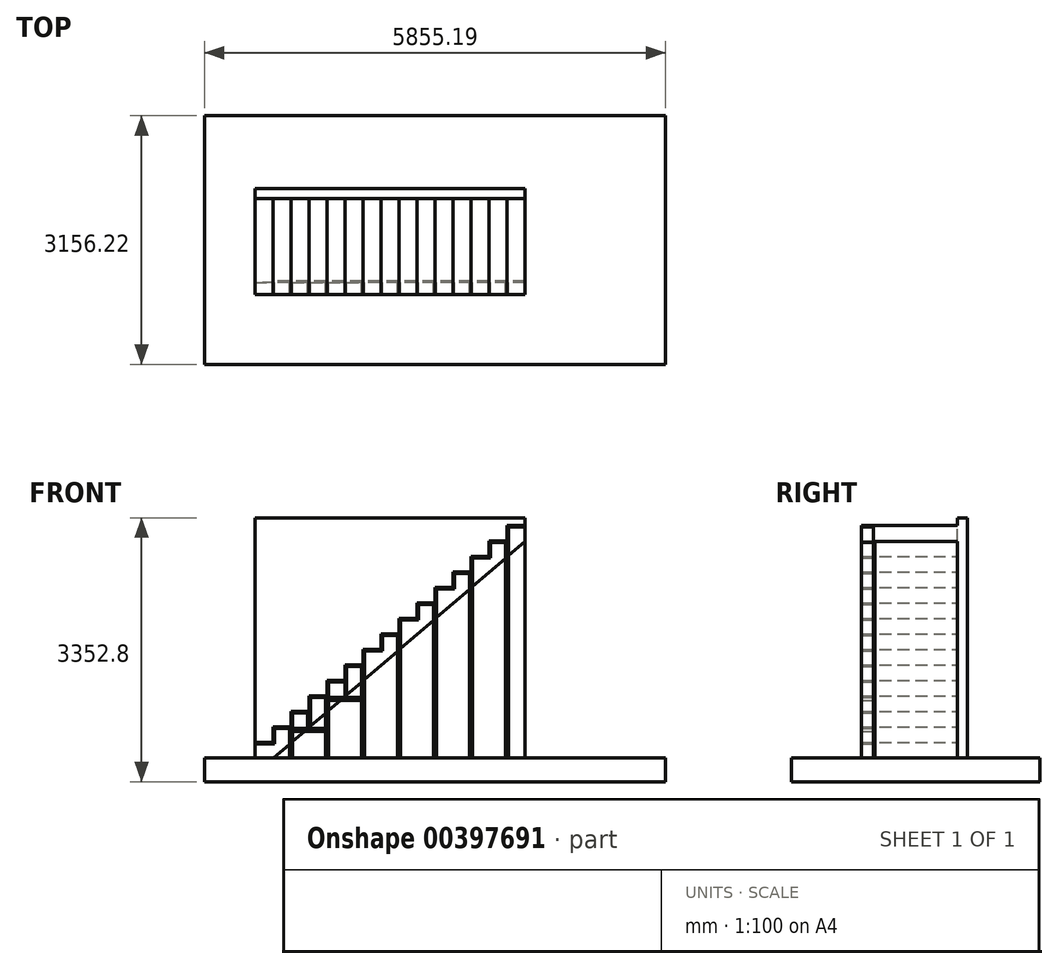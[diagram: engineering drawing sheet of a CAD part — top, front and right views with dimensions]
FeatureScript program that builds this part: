
annotation { "Feature Type Name" : "Feature", "Feature Type Description" : "" }
export const myFeature = defineFeature(function(context is Context, id is Id, definition is map)
    precondition{}
    {
        {
            var Q0;
            Q0=qCreatedBy(makeId("Front.planeOp"),FACE);
            var sketch = newSketch(context, id + "F0", { "sketchPlane" : qUnion([Q0])});
            skLineSegment(sketch, "E0", {"start": v(0, 0) * mm, "end": v(0, 196.85) * mm});
            skLineSegment(sketch, "E1", {"start": v(0, 196.85) * mm, "end": v(228.6, 196.85) * mm});
            skLineSegment(sketch, "E2", {"start": v(228.6, 196.85) * mm, "end": v(228.6, 393.7) * mm});
            skLineSegment(sketch, "E3", {"start": v(228.6, 393.7) * mm, "end": v(457.2, 393.7) * mm});
            skLineSegment(sketch, "E4", {"start": v(457.2, 393.7) * mm, "end": v(457.2, 590.55) * mm});
            skLineSegment(sketch, "E5", {"start": v(457.2, 590.55) * mm, "end": v(685.8, 590.55) * mm});
            skLineSegment(sketch, "E6", {"start": v(685.8, 590.55) * mm, "end": v(685.8, 787.4) * mm});
            skLineSegment(sketch, "E7", {"start": v(685.8, 787.4) * mm, "end": v(914.4, 787.4) * mm});
            skLineSegment(sketch, "E8", {"start": v(914.4, 787.4) * mm, "end": v(914.4, 984.25) * mm});
            skLineSegment(sketch, "E9", {"start": v(914.4, 984.25) * mm, "end": v(1143, 984.25) * mm});
            skLineSegment(sketch, "E10", {"start": v(1143, 984.25) * mm, "end": v(1143, 1181.1) * mm});
            skLineSegment(sketch, "E11", {"start": v(1143, 1181.1) * mm, "end": v(1371.6, 1181.1) * mm});
            skLineSegment(sketch, "E12", {"start": v(1371.6, 1181.1) * mm, "end": v(1371.6, 1377.95) * mm});
            skLineSegment(sketch, "E13", {"start": v(1371.6, 1377.95) * mm, "end": v(1600.2, 1377.95) * mm});
            skLineSegment(sketch, "E14", {"start": v(1600.2, 1377.95) * mm, "end": v(1600.2, 1574.8) * mm});
            skLineSegment(sketch, "E15", {"start": v(1600.2, 1574.8) * mm, "end": v(1828.8, 1574.8) * mm});
            skLineSegment(sketch, "E16", {"start": v(1828.8, 1574.8) * mm, "end": v(1828.8, 1771.65) * mm});
            skLineSegment(sketch, "E17", {"start": v(1828.8, 1771.65) * mm, "end": v(2057.4, 1771.65) * mm});
            skLineSegment(sketch, "E18", {"start": v(2057.4, 1771.65) * mm, "end": v(2057.4, 1968.5) * mm});
            skLineSegment(sketch, "E19", {"start": v(2057.4, 1968.5) * mm, "end": v(2286, 1968.5) * mm});
            skLineSegment(sketch, "E20", {"start": v(2286, 1968.5) * mm, "end": v(2286, 2165.35) * mm});
            skLineSegment(sketch, "E21", {"start": v(2286, 2165.35) * mm, "end": v(2514.6, 2165.35) * mm});
            skLineSegment(sketch, "E22", {"start": v(2514.6, 2165.35) * mm, "end": v(2514.6, 2362.2) * mm});
            skLineSegment(sketch, "E23", {"start": v(2514.6, 2362.2) * mm, "end": v(2743.2, 2362.2) * mm});
            skLineSegment(sketch, "E24", {"start": v(2743.2, 2362.2) * mm, "end": v(2743.2, 2559.05) * mm});
            skLineSegment(sketch, "E25", {"start": v(2743.2, 2559.05) * mm, "end": v(2971.8, 2559.05) * mm});
            skLineSegment(sketch, "E26", {"start": v(2971.8, 2559.05) * mm, "end": v(2971.8, 2755.9) * mm});
            skLineSegment(sketch, "E27", {"start": v(2971.8, 2755.9) * mm, "end": v(3200.4, 2755.9) * mm});
            skLineSegment(sketch, "E28", {"start": v(3200.4, 2755.9) * mm, "end": v(3200.4, 2952.75) * mm});
            skLineSegment(sketch, "E29", {"start": v(3200.4, 2952.75) * mm, "end": v(3429, 2952.75) * mm});
            skLineSegment(sketch, "E30", {"start": v(3429, 2952.75) * mm, "end": v(3429, 2747.37) * mm});
            skLineSegment(sketch, "E31", {"start": v(3200.4, 2952.75) * mm, "end": v(228.6, 393.7) * mm, "construction": true});
            skLineSegment(sketch, "E32", {"start": v(3429, 2747.37) * mm, "end": v(238.5, 0) * mm});
            skLineSegment(sketch, "E33", {"start": v(0, 0) * mm, "end": v(238.5, 0) * mm});
            skPoint(sketch, "E34.orphan", {"position": v(228.6, -8.53) * mm});
            skSolve(sketch);
        }
        {
            var Q0;
            Q0 = qSketchRegion(id + "F0", true);
            extrude(context, id + "F1", {"entities" : qUnion([Q0]), "depth" : 1066.8 * mm});
        }
        {
            var Q0;
            Q0=makeQuery(id+"F1.opExtrude","SWEPT_FACE",FACE,{"disambiguationData":[OSD([sQuery(id+"F0.wireOp",EDGE,"E33")])]});
            var sketch = newSketch(context, id + "F2", { "sketchPlane" : qUnion([Q0])});
            skLineSegment(sketch, "E35.bottom", {"start": v(0, 0) * mm, "end": v(3429, 0) * mm});
            skLineSegment(sketch, "E35.top", {"start": v(0, -127) * mm, "end": v(3429, -127) * mm});
            skLineSegment(sketch, "E35.left", {"start": v(0, 0) * mm, "end": v(0, -127) * mm});
            skLineSegment(sketch, "E35.right", {"start": v(3429, 0) * mm, "end": v(3429, -127) * mm});
            skSolve(sketch);
        }
        {
            var Q0;
            Q0=makeQuery(id+"F2.imprint","IMPRINT",FACE,{"disambiguationData":[TD([[makeQuery(id+"F2.imprint","IMPRINT",EDGE,{"derivedFrom":sQuery(id+"F2.wireOp",EDGE,"E35.top")}),1.0]])]});
            extrude(context, id + "F3", {"entities" : qUnion([Q0]), "operationType" : NewBodyOperationType.ADD, "oppositeDirection" : true, "depth" : 3048 * mm});
        }
        {
            var Q0;
            Q0=makeQuery(id+"F1.opExtrude","CAP_FACE",FACE,{"disambiguationData":[OSD([sQuery(id+"F0.wireOp",EDGE,"E0"),sQuery(id+"F0.wireOp",EDGE,"E1"),sQuery(id+"F0.wireOp",EDGE,"E2"),sQuery(id+"F0.wireOp",EDGE,"E3"),sQuery(id+"F0.wireOp",EDGE,"E4"),sQuery(id+"F0.wireOp",EDGE,"E5"),sQuery(id+"F0.wireOp",EDGE,"E6"),sQuery(id+"F0.wireOp",EDGE,"E7"),sQuery(id+"F0.wireOp",EDGE,"E8"),sQuery(id+"F0.wireOp",EDGE,"E9"),sQuery(id+"F0.wireOp",EDGE,"E10"),sQuery(id+"F0.wireOp",EDGE,"E11"),sQuery(id+"F0.wireOp",EDGE,"E12"),sQuery(id+"F0.wireOp",EDGE,"E13"),sQuery(id+"F0.wireOp",EDGE,"E14"),sQuery(id+"F0.wireOp",EDGE,"E15"),sQuery(id+"F0.wireOp",EDGE,"E16"),sQuery(id+"F0.wireOp",EDGE,"E17"),sQuery(id+"F0.wireOp",EDGE,"E18"),sQuery(id+"F0.wireOp",EDGE,"E19"),sQuery(id+"F0.wireOp",EDGE,"E20"),sQuery(id+"F0.wireOp",EDGE,"E21"),sQuery(id+"F0.wireOp",EDGE,"E22"),sQuery(id+"F0.wireOp",EDGE,"E23"),sQuery(id+"F0.wireOp",EDGE,"E24"),sQuery(id+"F0.wireOp",EDGE,"E25"),sQuery(id+"F0.wireOp",EDGE,"E26"),sQuery(id+"F0.wireOp",EDGE,"E27"),sQuery(id+"F0.wireOp",EDGE,"E28"),sQuery(id+"F0.wireOp",EDGE,"E29"),sQuery(id+"F0.wireOp",EDGE,"E30"),sQuery(id+"F0.wireOp",EDGE,"E32"),sQuery(id+"F0.wireOp",EDGE,"E33")])],"isStart":false});
            var sketch = newSketch(context, id + "F4", { "sketchPlane" : qUnion([Q0])});
            skLineSegment(sketch, "E36", {"start": v(238.5, 0) * mm, "end": v(3429, 2747.37) * mm});
            skLineSegment(sketch, "E37", {"start": v(3429, 2747.37) * mm, "end": v(3429, 0) * mm});
            skLineSegment(sketch, "E38", {"start": v(3429, 0) * mm, "end": v(238.5, 0) * mm});
            skSolve(sketch);
        }
        {
            var Q0;
            Q0=makeQuery(id+"F4.imprint","IMPRINT",FACE,{"disambiguationData":[TD([[makeQuery(id+"F4.imprint","IMPRINT",EDGE,{"derivedFrom":sQuery(id+"F4.wireOp",EDGE,"E36")}),1.0]])]});
            extrude(context, id + "F5", {"entities" : qUnion([Q0]), "oppositeDirection" : true, "depth" : 19.05 * mm});
        }
        {
            var Q0;
            Q0=makeQuery(id+"F1.opExtrude","CAP_FACE",FACE,{"disambiguationData":[OSD([sQuery(id+"F0.wireOp",EDGE,"E0"),sQuery(id+"F0.wireOp",EDGE,"E1"),sQuery(id+"F0.wireOp",EDGE,"E2"),sQuery(id+"F0.wireOp",EDGE,"E3"),sQuery(id+"F0.wireOp",EDGE,"E4"),sQuery(id+"F0.wireOp",EDGE,"E5"),sQuery(id+"F0.wireOp",EDGE,"E6"),sQuery(id+"F0.wireOp",EDGE,"E7"),sQuery(id+"F0.wireOp",EDGE,"E8"),sQuery(id+"F0.wireOp",EDGE,"E9"),sQuery(id+"F0.wireOp",EDGE,"E10"),sQuery(id+"F0.wireOp",EDGE,"E11"),sQuery(id+"F0.wireOp",EDGE,"E12"),sQuery(id+"F0.wireOp",EDGE,"E13"),sQuery(id+"F0.wireOp",EDGE,"E14"),sQuery(id+"F0.wireOp",EDGE,"E15"),sQuery(id+"F0.wireOp",EDGE,"E16"),sQuery(id+"F0.wireOp",EDGE,"E17"),sQuery(id+"F0.wireOp",EDGE,"E18"),sQuery(id+"F0.wireOp",EDGE,"E19"),sQuery(id+"F0.wireOp",EDGE,"E20"),sQuery(id+"F0.wireOp",EDGE,"E21"),sQuery(id+"F0.wireOp",EDGE,"E22"),sQuery(id+"F0.wireOp",EDGE,"E23"),sQuery(id+"F0.wireOp",EDGE,"E24"),sQuery(id+"F0.wireOp",EDGE,"E25"),sQuery(id+"F0.wireOp",EDGE,"E26"),sQuery(id+"F0.wireOp",EDGE,"E27"),sQuery(id+"F0.wireOp",EDGE,"E28"),sQuery(id+"F0.wireOp",EDGE,"E29"),sQuery(id+"F0.wireOp",EDGE,"E30"),sQuery(id+"F0.wireOp",EDGE,"E32"),sQuery(id+"F0.wireOp",EDGE,"E33")])],"isStart":false});
            var sketch = newSketch(context, id + "F6", { "sketchPlane" : qUnion([Q0])});
            skLineSegment(sketch, "E39", {"start": v(0, 0) * mm, "end": v(0, 196.85) * mm});
            skLineSegment(sketch, "E40", {"start": v(0, 196.85) * mm, "end": v(228.6, 196.85) * mm});
            skLineSegment(sketch, "E41", {"start": v(228.6, 196.85) * mm, "end": v(228.6, 393.7) * mm});
            skLineSegment(sketch, "E42", {"start": v(228.6, 393.7) * mm, "end": v(457.2, 393.7) * mm});
            skLineSegment(sketch, "E43", {"start": v(457.2, 393.7) * mm, "end": v(457.2, 590.55) * mm});
            skLineSegment(sketch, "E44", {"start": v(457.2, 590.55) * mm, "end": v(685.8, 590.55) * mm});
            skLineSegment(sketch, "E45", {"start": v(685.8, 590.55) * mm, "end": v(685.8, 787.4) * mm});
            skLineSegment(sketch, "E46", {"start": v(685.8, 787.4) * mm, "end": v(914.4, 787.4) * mm});
            skLineSegment(sketch, "E47", {"start": v(914.4, 787.4) * mm, "end": v(914.4, 984.25) * mm});
            skLineSegment(sketch, "E48", {"start": v(914.4, 984.25) * mm, "end": v(1143, 984.25) * mm});
            skLineSegment(sketch, "E49", {"start": v(1143, 984.25) * mm, "end": v(1143, 1181.1) * mm});
            skLineSegment(sketch, "E50", {"start": v(1143, 1181.1) * mm, "end": v(1371.6, 1181.1) * mm});
            skLineSegment(sketch, "E51", {"start": v(1371.6, 1181.1) * mm, "end": v(1371.6, 1377.95) * mm});
            skLineSegment(sketch, "E52", {"start": v(1371.6, 1377.95) * mm, "end": v(1600.2, 1377.95) * mm});
            skLineSegment(sketch, "E53", {"start": v(1600.2, 1377.95) * mm, "end": v(1600.2, 1574.8) * mm});
            skLineSegment(sketch, "E54", {"start": v(1600.2, 1574.8) * mm, "end": v(1828.8, 1574.8) * mm});
            skLineSegment(sketch, "E55", {"start": v(1828.8, 1574.8) * mm, "end": v(1828.8, 1771.65) * mm});
            skLineSegment(sketch, "E56", {"start": v(1828.8, 1771.65) * mm, "end": v(2057.4, 1771.65) * mm});
            skLineSegment(sketch, "E57", {"start": v(2057.4, 1771.65) * mm, "end": v(2057.4, 1968.5) * mm});
            skLineSegment(sketch, "E58", {"start": v(2057.4, 1968.5) * mm, "end": v(2286, 1968.5) * mm});
            skLineSegment(sketch, "E59", {"start": v(2286, 1968.5) * mm, "end": v(2286, 2165.35) * mm});
            skLineSegment(sketch, "E60", {"start": v(2286, 2165.35) * mm, "end": v(2514.6, 2165.35) * mm});
            skLineSegment(sketch, "E61", {"start": v(2514.6, 2165.35) * mm, "end": v(2514.6, 2362.2) * mm});
            skLineSegment(sketch, "E62", {"start": v(2514.6, 2362.2) * mm, "end": v(2743.2, 2362.2) * mm});
            skLineSegment(sketch, "E63", {"start": v(2743.2, 2362.2) * mm, "end": v(2743.2, 2559.05) * mm});
            skLineSegment(sketch, "E64", {"start": v(2743.2, 2559.05) * mm, "end": v(2971.8, 2559.05) * mm});
            skLineSegment(sketch, "E65", {"start": v(2971.8, 2559.05) * mm, "end": v(2971.8, 2755.9) * mm});
            skLineSegment(sketch, "E66", {"start": v(2971.8, 2755.9) * mm, "end": v(3200.4, 2755.9) * mm});
            skLineSegment(sketch, "E67", {"start": v(3200.4, 2755.9) * mm, "end": v(3200.4, 2952.75) * mm});
            skLineSegment(sketch, "E68", {"start": v(3200.4, 2952.75) * mm, "end": v(3429, 2952.75) * mm});
            skSolve(sketch);
        }
        {
            var Q0;
            Q0=makeQuery(id+"F6.imprint","IMPRINT",FACE,{"disambiguationData":[TD([[makeQuery(id+"F6.imprint","IMPRINT",EDGE,{"derivedFrom":sQuery(id+"F6.wireOp",EDGE,"E39")}),-1.0]])]});
            var sketch = newSketch(context, id + "F7", { "sketchPlane" : qUnion([Q0])});
            skLineSegment(sketch, "E69.0", {"start": v(0, 196.85) * mm, "end": v(228.6, 196.85) * mm});
            skLineSegment(sketch, "E70.0", {"start": v(228.6, 196.85) * mm, "end": v(228.6, 393.7) * mm});
            skLineSegment(sketch, "E71.0", {"start": v(228.6, 393.7) * mm, "end": v(457.2, 393.7) * mm});
            skLineSegment(sketch, "E72.0", {"start": v(457.2, 393.7) * mm, "end": v(457.2, 590.55) * mm});
            skLineSegment(sketch, "E73.0", {"start": v(457.2, 590.55) * mm, "end": v(685.8, 590.55) * mm});
            skLineSegment(sketch, "E74.0", {"start": v(685.8, 590.55) * mm, "end": v(685.8, 787.4) * mm});
            skLineSegment(sketch, "E75.0", {"start": v(685.8, 787.4) * mm, "end": v(914.4, 787.4) * mm});
            skLineSegment(sketch, "E76.0", {"start": v(914.4, 787.4) * mm, "end": v(914.4, 984.25) * mm});
            skLineSegment(sketch, "E77.0", {"start": v(914.4, 984.25) * mm, "end": v(1143, 984.25) * mm});
            skLineSegment(sketch, "E78.0", {"start": v(1143, 984.25) * mm, "end": v(1143, 1181.1) * mm});
            skLineSegment(sketch, "E79.0", {"start": v(1143, 1181.1) * mm, "end": v(1371.6, 1181.1) * mm});
            skLineSegment(sketch, "E80.0", {"start": v(1371.6, 1181.1) * mm, "end": v(1371.6, 1377.95) * mm});
            skLineSegment(sketch, "E81.0", {"start": v(1371.6, 1377.95) * mm, "end": v(1600.2, 1377.95) * mm});
            skLineSegment(sketch, "E82.0", {"start": v(1600.2, 1377.95) * mm, "end": v(1600.2, 1574.8) * mm});
            skLineSegment(sketch, "E83.0", {"start": v(1600.2, 1574.8) * mm, "end": v(1828.8, 1574.8) * mm});
            skLineSegment(sketch, "E84.0", {"start": v(1828.8, 1574.8) * mm, "end": v(1828.8, 1771.65) * mm});
            skLineSegment(sketch, "E85.0", {"start": v(1828.8, 1771.65) * mm, "end": v(2057.4, 1771.65) * mm});
            skLineSegment(sketch, "E86.0", {"start": v(2057.4, 1771.65) * mm, "end": v(2057.4, 1968.5) * mm});
            skLineSegment(sketch, "E87.0", {"start": v(2057.4, 1968.5) * mm, "end": v(2286, 1968.5) * mm});
            skLineSegment(sketch, "E88.0", {"start": v(2286, 1968.5) * mm, "end": v(2286, 2165.35) * mm});
            skLineSegment(sketch, "E89.0", {"start": v(2286, 2165.35) * mm, "end": v(2514.6, 2165.35) * mm});
            skLineSegment(sketch, "E90.0", {"start": v(2514.6, 2165.35) * mm, "end": v(2514.6, 2362.2) * mm});
            skLineSegment(sketch, "E91.0", {"start": v(2514.6, 2362.2) * mm, "end": v(2743.2, 2362.2) * mm});
            skLineSegment(sketch, "E92.0", {"start": v(2743.2, 2362.2) * mm, "end": v(2743.2, 2559.05) * mm});
            skLineSegment(sketch, "E93.0", {"start": v(2743.2, 2559.05) * mm, "end": v(2971.8, 2559.05) * mm});
            skLineSegment(sketch, "E94.0", {"start": v(2971.8, 2559.05) * mm, "end": v(2971.8, 2755.9) * mm});
            skLineSegment(sketch, "E95.0", {"start": v(2971.8, 2755.9) * mm, "end": v(3200.4, 2755.9) * mm});
            skLineSegment(sketch, "E96.0", {"start": v(3200.4, 2755.9) * mm, "end": v(3200.4, 2952.75) * mm});
            skLineSegment(sketch, "E97.0", {"start": v(3200.4, 2952.75) * mm, "end": v(3429, 2952.75) * mm});
            skLineSegment(sketch, "E98", {"start": v(3429, 2952.75) * mm, "end": v(3429, 2933.7) * mm});
            skLineSegment(sketch, "E99", {"start": v(3429, 2933.7) * mm, "end": v(3219.45, 2933.7) * mm});
            skLineSegment(sketch, "E100", {"start": v(3219.45, 2933.7) * mm, "end": v(3219.45, 2736.85) * mm});
            skLineSegment(sketch, "E101", {"start": v(3219.45, 2736.85) * mm, "end": v(2990.85, 2736.85) * mm});
            skLineSegment(sketch, "E102", {"start": v(2990.85, 2736.85) * mm, "end": v(2990.85, 2540) * mm});
            skLineSegment(sketch, "E103", {"start": v(2990.85, 2540) * mm, "end": v(2762.25, 2540) * mm});
            skLineSegment(sketch, "E104", {"start": v(2762.25, 2540) * mm, "end": v(2762.25, 2343.15) * mm});
            skLineSegment(sketch, "E105", {"start": v(2762.25, 2343.15) * mm, "end": v(2533.65, 2343.15) * mm});
            skLineSegment(sketch, "E106", {"start": v(2533.65, 2343.15) * mm, "end": v(2533.65, 2146.3) * mm});
            skLineSegment(sketch, "E107", {"start": v(2533.65, 2146.3) * mm, "end": v(2305.05, 2146.3) * mm});
            skLineSegment(sketch, "E108", {"start": v(2305.05, 2146.3) * mm, "end": v(2305.05, 1949.45) * mm});
            skLineSegment(sketch, "E109", {"start": v(2305.05, 1949.45) * mm, "end": v(2076.45, 1949.45) * mm});
            skLineSegment(sketch, "E110", {"start": v(2076.45, 1949.45) * mm, "end": v(2076.45, 1752.6) * mm});
            skLineSegment(sketch, "E111", {"start": v(2076.45, 1752.6) * mm, "end": v(1847.85, 1752.6) * mm});
            skLineSegment(sketch, "E112", {"start": v(1847.85, 1752.6) * mm, "end": v(1847.85, 1555.75) * mm});
            skLineSegment(sketch, "E113", {"start": v(1847.85, 1555.75) * mm, "end": v(1619.25, 1555.75) * mm});
            skLineSegment(sketch, "E114", {"start": v(1619.25, 1555.75) * mm, "end": v(1619.25, 1358.9) * mm});
            skLineSegment(sketch, "E115", {"start": v(1619.25, 1358.9) * mm, "end": v(1390.65, 1358.9) * mm});
            skLineSegment(sketch, "E116", {"start": v(1390.65, 1358.9) * mm, "end": v(1390.65, 1162.05) * mm});
            skLineSegment(sketch, "E117", {"start": v(1390.65, 1162.05) * mm, "end": v(1162.05, 1162.05) * mm});
            skLineSegment(sketch, "E118", {"start": v(1162.05, 1162.05) * mm, "end": v(1162.05, 965.2) * mm});
            skLineSegment(sketch, "E119", {"start": v(1162.05, 965.2) * mm, "end": v(933.45, 965.2) * mm});
            skLineSegment(sketch, "E120", {"start": v(933.45, 965.2) * mm, "end": v(933.45, 768.35) * mm});
            skLineSegment(sketch, "E121", {"start": v(933.45, 768.35) * mm, "end": v(704.85, 768.35) * mm});
            skLineSegment(sketch, "E122", {"start": v(704.85, 768.35) * mm, "end": v(704.85, 571.5) * mm});
            skLineSegment(sketch, "E123", {"start": v(704.85, 571.5) * mm, "end": v(476.25, 571.5) * mm});
            skLineSegment(sketch, "E124", {"start": v(476.25, 571.5) * mm, "end": v(476.25, 374.65) * mm});
            skLineSegment(sketch, "E125", {"start": v(476.25, 374.65) * mm, "end": v(247.65, 374.65) * mm});
            skLineSegment(sketch, "E126", {"start": v(247.65, 374.65) * mm, "end": v(247.65, 177.8) * mm});
            skLineSegment(sketch, "E127", {"start": v(247.65, 177.8) * mm, "end": v(0, 177.8) * mm});
            skLineSegment(sketch, "E128", {"start": v(0, 177.8) * mm, "end": v(0, 196.85) * mm});
            skSolve(sketch);
        }
        {
            var Q0;
            Q0 = qSketchRegion(id + "F7", true);
            extrude(context, id + "F8", {"entities" : qUnion([Q0]), "operationType" : NewBodyOperationType.ADD, "depth" : 152.4 * mm});
        }
        {
            var Q0;
            Q0=makeQuery(id+"F6.imprint","IMPRINT",FACE,{"disambiguationData":[TD([[makeQuery(id+"F6.imprint","IMPRINT",EDGE,{"derivedFrom":sQuery(id+"F6.wireOp",EDGE,"E39")}),-1.0]])]});
            var sketch = newSketch(context, id + "F9", { "sketchPlane" : qUnion([Q0])});
            skLineSegment(sketch, "E129.bottom", {"start": v(438.15, 374.65) * mm, "end": v(476.25, 374.65) * mm});
            skLineSegment(sketch, "E129.top", {"start": v(438.15, 0) * mm, "end": v(476.25, 0) * mm});
            skLineSegment(sketch, "E129.left", {"start": v(438.15, 374.65) * mm, "end": v(438.15, 0) * mm});
            skLineSegment(sketch, "E129.right", {"start": v(476.25, 374.65) * mm, "end": v(476.25, 0) * mm});
            skLineSegment(sketch, "E130.bottom", {"start": v(895.35, 768.35) * mm, "end": v(933.45, 768.35) * mm});
            skLineSegment(sketch, "E130.top", {"start": v(895.35, 0) * mm, "end": v(933.45, 0) * mm});
            skLineSegment(sketch, "E130.left", {"start": v(895.35, 768.35) * mm, "end": v(895.35, 0) * mm});
            skLineSegment(sketch, "E130.right", {"start": v(933.45, 768.35) * mm, "end": v(933.45, 0) * mm});
            skLineSegment(sketch, "E131.bottom", {"start": v(1352.55, 1162.05) * mm, "end": v(1390.65, 1162.05) * mm});
            skLineSegment(sketch, "E131.top", {"start": v(1352.55, 0) * mm, "end": v(1390.65, 0) * mm});
            skLineSegment(sketch, "E131.left", {"start": v(1352.55, 1162.05) * mm, "end": v(1352.55, 0) * mm});
            skLineSegment(sketch, "E131.right", {"start": v(1390.65, 1162.05) * mm, "end": v(1390.65, 0) * mm});
            skLineSegment(sketch, "E132.bottom", {"start": v(1809.75, 1555.75) * mm, "end": v(1847.85, 1555.75) * mm});
            skLineSegment(sketch, "E132.top", {"start": v(1809.75, 0) * mm, "end": v(1847.85, 0) * mm});
            skLineSegment(sketch, "E132.left", {"start": v(1809.75, 1555.75) * mm, "end": v(1809.75, 0) * mm});
            skLineSegment(sketch, "E132.right", {"start": v(1847.85, 1555.75) * mm, "end": v(1847.85, 0) * mm});
            skLineSegment(sketch, "E133.bottom", {"start": v(2266.95, 1949.45) * mm, "end": v(2305.05, 1949.45) * mm});
            skLineSegment(sketch, "E133.top", {"start": v(2266.95, 0) * mm, "end": v(2305.05, 0) * mm});
            skLineSegment(sketch, "E133.left", {"start": v(2266.95, 1949.45) * mm, "end": v(2266.95, 0) * mm});
            skLineSegment(sketch, "E133.right", {"start": v(2305.05, 1949.45) * mm, "end": v(2305.05, 0) * mm});
            skLineSegment(sketch, "E134.bottom", {"start": v(2724.15, 2343.15) * mm, "end": v(2762.25, 2343.15) * mm});
            skLineSegment(sketch, "E134.top", {"start": v(2724.15, 0) * mm, "end": v(2762.25, 0) * mm});
            skLineSegment(sketch, "E134.left", {"start": v(2724.15, 2343.15) * mm, "end": v(2724.15, 0) * mm});
            skLineSegment(sketch, "E134.right", {"start": v(2762.25, 2343.15) * mm, "end": v(2762.25, 0) * mm});
            skLineSegment(sketch, "E135.bottom", {"start": v(3181.35, 2736.85) * mm, "end": v(3219.45, 2736.85) * mm});
            skLineSegment(sketch, "E135.top", {"start": v(3181.35, 0) * mm, "end": v(3219.45, 0) * mm});
            skLineSegment(sketch, "E135.left", {"start": v(3181.35, 2736.85) * mm, "end": v(3181.35, 0) * mm});
            skLineSegment(sketch, "E135.right", {"start": v(3219.45, 2736.85) * mm, "end": v(3219.45, 0) * mm});
            skSolve(sketch);
        }
        {
            var Q0;
            Q0 = qSketchRegion(id + "F9", true);
            extrude(context, id + "F10", {"entities" : qUnion([Q0]), "depth" : 152.4 * mm});
        }
        {
            var Q0;
            Q0=makeQuery(id+"F5.opExtrude","CAP_FACE",FACE,{"disambiguationData":[OSD([sQuery(id+"F4.wireOp",EDGE,"E36"),sQuery(id+"F4.wireOp",EDGE,"E37"),sQuery(id+"F4.wireOp",EDGE,"E38")])],"isStart":true});
            var sketch = newSketch(context, id + "F11", { "sketchPlane" : qUnion([Q0])});
            skLineSegment(sketch, "E136.bottom", {"start": v(476.25, 374.65) * mm, "end": v(895.35, 374.65) * mm});
            skLineSegment(sketch, "E136.top", {"start": v(476.25, 336.55) * mm, "end": v(895.35, 336.55) * mm});
            skLineSegment(sketch, "E136.left", {"start": v(476.25, 374.65) * mm, "end": v(476.25, 336.55) * mm});
            skLineSegment(sketch, "E136.right", {"start": v(895.35, 374.65) * mm, "end": v(895.35, 336.55) * mm});
            skLineSegment(sketch, "E137.bottom", {"start": v(933.45, 768.35) * mm, "end": v(1352.55, 768.35) * mm});
            skLineSegment(sketch, "E137.top", {"start": v(933.45, 730.25) * mm, "end": v(1352.55, 730.25) * mm});
            skLineSegment(sketch, "E137.left", {"start": v(933.45, 768.35) * mm, "end": v(933.45, 730.25) * mm});
            skLineSegment(sketch, "E137.right", {"start": v(1352.55, 768.35) * mm, "end": v(1352.55, 730.25) * mm});
            skSolve(sketch);
        }
        {
            var Q0;
            Q0 = qSketchRegion(id + "F11", true);
            extrude(context, id + "F12", {"entities" : qUnion([Q0]), "depth" : 152.4 * mm});
        }
        {
            var Q0;
            Q0=makeQuery(id+"F3.boolean.opBoolean","MERGE",FACE,{"derivedFrom":[makeQuery(id+"F1.opExtrude","SWEPT_FACE",FACE,{"disambiguationData":[OSD([sQuery(id+"F0.wireOp",EDGE,"E33")])]}),makeQuery(id+"F3.opExtrude","CAP_FACE",FACE,{"disambiguationData":[OSD([sQuery(id+"F2.wireOp",EDGE,"E35.bottom"),sQuery(id+"F2.wireOp",EDGE,"E35.top"),sQuery(id+"F2.wireOp",EDGE,"E35.left"),sQuery(id+"F2.wireOp",EDGE,"E35.right")])],"isStart":true})]});
            var sketch = newSketch(context, id + "F13", { "sketchPlane" : qUnion([Q0])});
            skLineSegment(sketch, "E138.bottom", {"start": v(-639.5, 2105.14) * mm, "end": v(5215.68, 2105.14) * mm});
            skLineSegment(sketch, "E138.top", {"start": v(-639.5, -1051.08) * mm, "end": v(5215.68, -1051.08) * mm});
            skLineSegment(sketch, "E138.left", {"start": v(-639.5, 2105.14) * mm, "end": v(-639.5, -1051.08) * mm});
            skLineSegment(sketch, "E138.right", {"start": v(5215.68, 2105.14) * mm, "end": v(5215.68, -1051.08) * mm});
            skSolve(sketch);
        }
        {
            var Q0;
            Q0 = qSketchRegion(id + "F13", true);
            extrude(context, id + "F14", {"entities" : qUnion([Q0]), "depth" : 304.8 * mm});
        }
        {
            var Q0;
            Q0=makeQuery(id+"F6.imprint","IMPRINT",FACE,{"disambiguationData":[TD([[makeQuery(id+"F6.imprint","IMPRINT",EDGE,{"derivedFrom":sQuery(id+"F6.wireOp",EDGE,"E39")}),-1.0]])]});
            var sketch = newSketch(context, id + "F15", { "sketchPlane" : qUnion([Q0])});
            skLineSegment(sketch, "E139.bottom", {"start": v(666.75, 571.5) * mm, "end": v(704.85, 571.5) * mm});
            skLineSegment(sketch, "E139.top", {"start": v(666.75, 374.65) * mm, "end": v(704.85, 374.65) * mm});
            skLineSegment(sketch, "E139.left", {"start": v(666.75, 571.5) * mm, "end": v(666.75, 374.65) * mm});
            skLineSegment(sketch, "E139.right", {"start": v(704.85, 571.5) * mm, "end": v(704.85, 374.65) * mm});
            skLineSegment(sketch, "E140.bottom", {"start": v(1143, 965.2) * mm, "end": v(1162.05, 965.2) * mm});
            skLineSegment(sketch, "E140.top", {"start": v(1143, 768.35) * mm, "end": v(1162.05, 768.35) * mm});
            skLineSegment(sketch, "E140.left", {"start": v(1143, 965.2) * mm, "end": v(1143, 768.35) * mm});
            skLineSegment(sketch, "E140.right", {"start": v(1162.05, 965.2) * mm, "end": v(1162.05, 768.35) * mm});
            skSolve(sketch);
        }
        {
            var Q0;
            Q0 = qSketchRegion(id + "F15", true);
            extrude(context, id + "F16", {"entities" : qUnion([Q0]), "depth" : 152.4 * mm});
        }
    });
